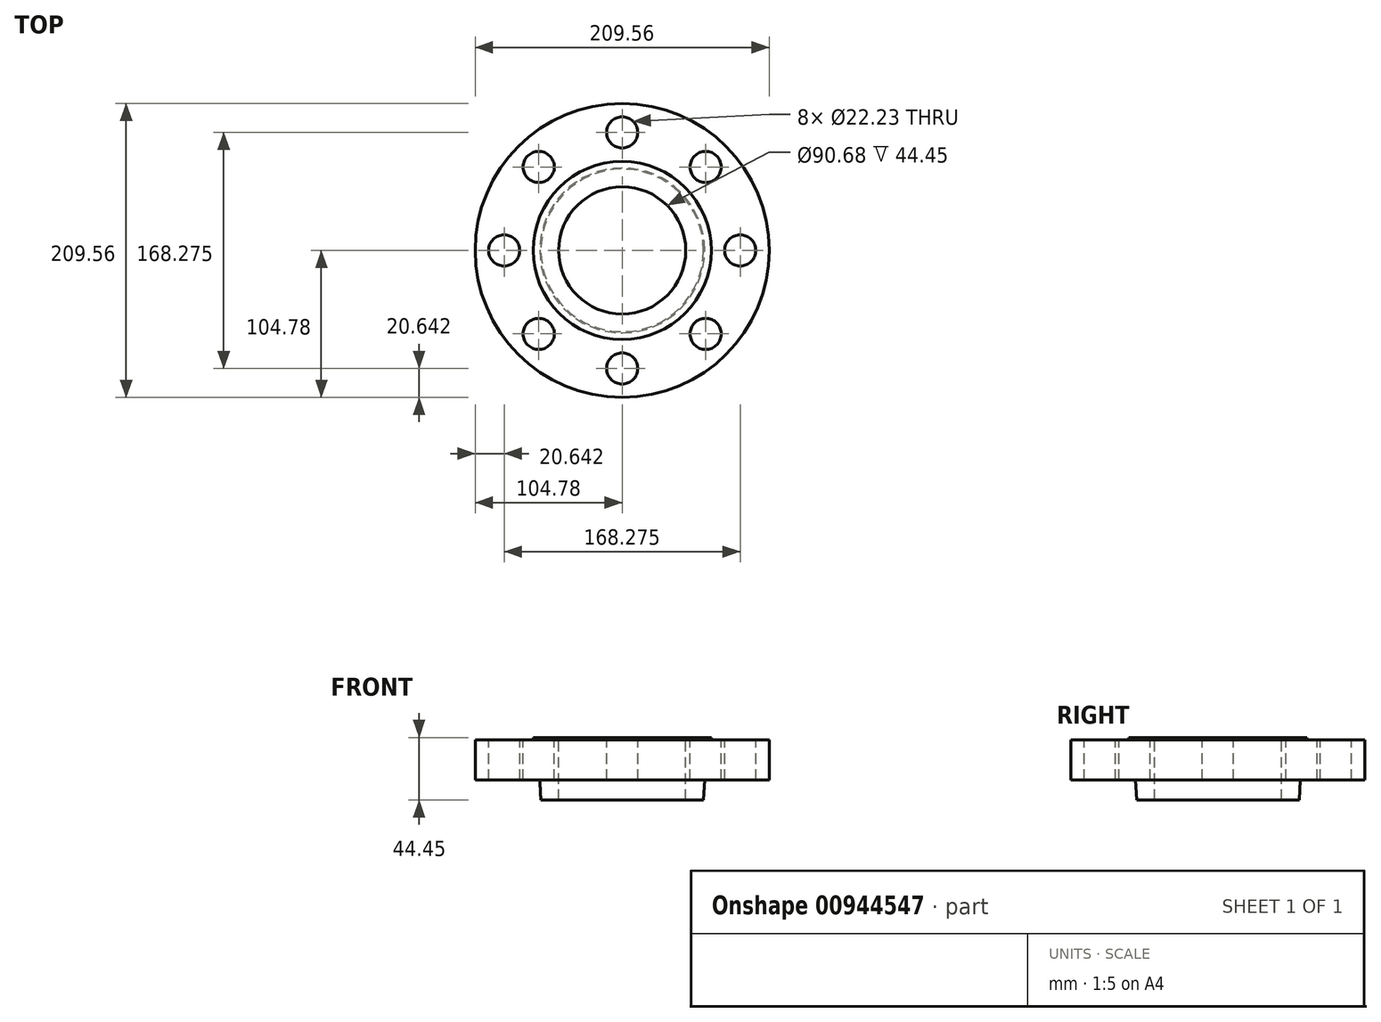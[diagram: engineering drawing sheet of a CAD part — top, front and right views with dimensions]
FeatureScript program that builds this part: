
annotation { "Feature Type Name" : "Feature", "Feature Type Description" : "" }
export const myFeature = defineFeature(function(context is Context, id is Id, definition is map)
    precondition{}
    {
        {
            var Q0;
            Q0=qCreatedBy(makeId("Top.planeOp"),FACE);
            var sketch = newSketch(context, id + "F0", { "sketchPlane" : qUnion([Q0])});
            skCircle(sketch, "E0", {"center": v(0, 0) * mm, "radius": 104.78 * mm});
            skSolve(sketch);
        }
        {
            var Q0;
            Q0 = qSketchRegion(id + "F0", true);
            extrude(context, id + "F1", {"entities" : qUnion([Q0]), "oppositeDirection" : true, "depth" : 28.57 * mm, "offsetDistance" : 25 * mm});
        }
        {
            var Q0;
            Q0=makeQuery(id+"F1.opExtrude","CAP_FACE",FACE,{"disambiguationData":[OSD([sQuery(id+"F0.wireOp",EDGE,"E0")])],"isStart":true});
            var sketch = newSketch(context, id + "F2", { "sketchPlane" : qUnion([Q0])});
            skCircle(sketch, "E1", {"center": v(0, 0) * mm, "radius": 63.5 * mm});
            skSolve(sketch);
        }
        {
            var Q0;
            Q0 = qSketchRegion(id + "F2", true);
            extrude(context, id + "F3", {"entities" : qUnion([Q0]), "operationType" : NewBodyOperationType.ADD, "depth" : 1.59 * mm, "offsetDistance" : 25 * mm});
        }
        {
            var Q0;
            Q0=makeQuery(id+"F1.opExtrude","CAP_FACE",FACE,{"disambiguationData":[OSD([sQuery(id+"F0.wireOp",EDGE,"E0")])],"isStart":false});
            var sketch = newSketch(context, id + "F4", { "sketchPlane" : qUnion([Q0])});
            skCircle(sketch, "E2", {"center": v(0, 0) * mm, "radius": 58.74 * mm});
            skSolve(sketch);
        }
        {
            var Q0;
            Q0 = qSketchRegion(id + "F4", true);
            extrude(context, id + "F5", {"entities" : qUnion([Q0]), "operationType" : NewBodyOperationType.ADD, "depth" : 14.29 * mm, "offsetDistance" : 25 * mm, "hasDraft" : true, "draftAngle" : 3 * degree, "draftPullDirection" : true});
        }
        {
            var Q0;
            Q0=makeQuery(id+"F3.opExtrude","CAP_FACE",FACE,{"disambiguationData":[OSD([sQuery(id+"F2.wireOp",EDGE,"E1")])],"isStart":false});
            var sketch = newSketch(context, id + "F6", { "sketchPlane" : qUnion([Q0])});
            skCircle(sketch, "E3", {"center": v(0, 0) * mm, "radius": 45.34 * mm});
            skSolve(sketch);
        }
        {
            var Q0;
            Q0 = qSketchRegion(id + "F6", true);
            extrude(context, id + "F7", {"entities" : qUnion([Q0]), "operationType" : NewBodyOperationType.REMOVE, "endBound" : BoundingType.THROUGH_ALL, "oppositeDirection" : true, "depth" : 25 * mm, "offsetDistance" : 25 * mm});
        }
        {
            var Q0;
            Q0=makeQuery(id+"F1.opExtrude","CAP_FACE",FACE,{"disambiguationData":[OSD([sQuery(id+"F0.wireOp",EDGE,"E0")])],"isStart":true});
            var sketch = newSketch(context, id + "F8", { "sketchPlane" : qUnion([Q0])});
            skCircle(sketch, "E4", {"center": v(0, 0) * mm, "radius": 84.14 * mm});
            skCircle(sketch, "E5", {"center": v(84.14, 0) * mm, "radius": 11.11 * mm});
            skCircle(sketch, "E6.1.0", {"center": v(59.5, 59.5) * mm, "radius": 11.11 * mm});
            skCircle(sketch, "E6.2.0", {"center": v(0, 84.14) * mm, "radius": 11.11 * mm});
            skCircle(sketch, "E6.3.0", {"center": v(-59.5, 59.5) * mm, "radius": 11.11 * mm});
            skCircle(sketch, "E6.4.0", {"center": v(-84.14, 0) * mm, "radius": 11.11 * mm});
            skCircle(sketch, "E6.5.0", {"center": v(-59.5, -59.5) * mm, "radius": 11.11 * mm});
            skCircle(sketch, "E6.6.0", {"center": v(0, -84.14) * mm, "radius": 11.11 * mm});
            skCircle(sketch, "E6.7.0", {"center": v(59.5, -59.5) * mm, "radius": 11.11 * mm});
            skSolve(sketch);
        }
        {
            var Q0;
            Q0=sQuery(id+"F8.wireOp",VERTEX,"E5.center");
            var Q1;
            Q1=sQuery(id+"F8.wireOp",VERTEX,"E6.1.0.center");
            var Q2;
            Q2=sQuery(id+"F8.wireOp",VERTEX,"E6.2.0.center");
            var Q3;
            Q3=sQuery(id+"F8.wireOp",VERTEX,"E6.3.0.center");
            var Q4;
            Q4=sQuery(id+"F8.wireOp",VERTEX,"E6.4.0.center");
            var Q5;
            Q5=sQuery(id+"F8.wireOp",VERTEX,"E6.5.0.center");
            var Q6;
            Q6=sQuery(id+"F8.wireOp",VERTEX,"E6.6.0.center");
            var Q7;
            Q7=sQuery(id+"F8.wireOp",VERTEX,"E6.7.0.center");
            var Q8;
            Q8=makeQuery(id+"F1.opExtrude","SWEPT_BODY",BODY,{"disambiguationData":[OSD([sQuery(id+"F0.wireOp",EDGE,"E0")])]});
            hole(context, id + "F9", {"style" : HoleStyle.SIMPLE, "endStyle" : HoleEndStyle.THROUGH, "holeDiameter" : 22.23 * mm, "majorDiameter" : 5 * mm, "isTappedThrough" : true, "tappedDepth" : 12 * mm, "tapClearance" : 3, "locations" : qUnion([Q0, Q1, Q2, Q3, Q4, Q5, Q6, Q7]), "scope" : qUnion([Q8])});
        }
    });
